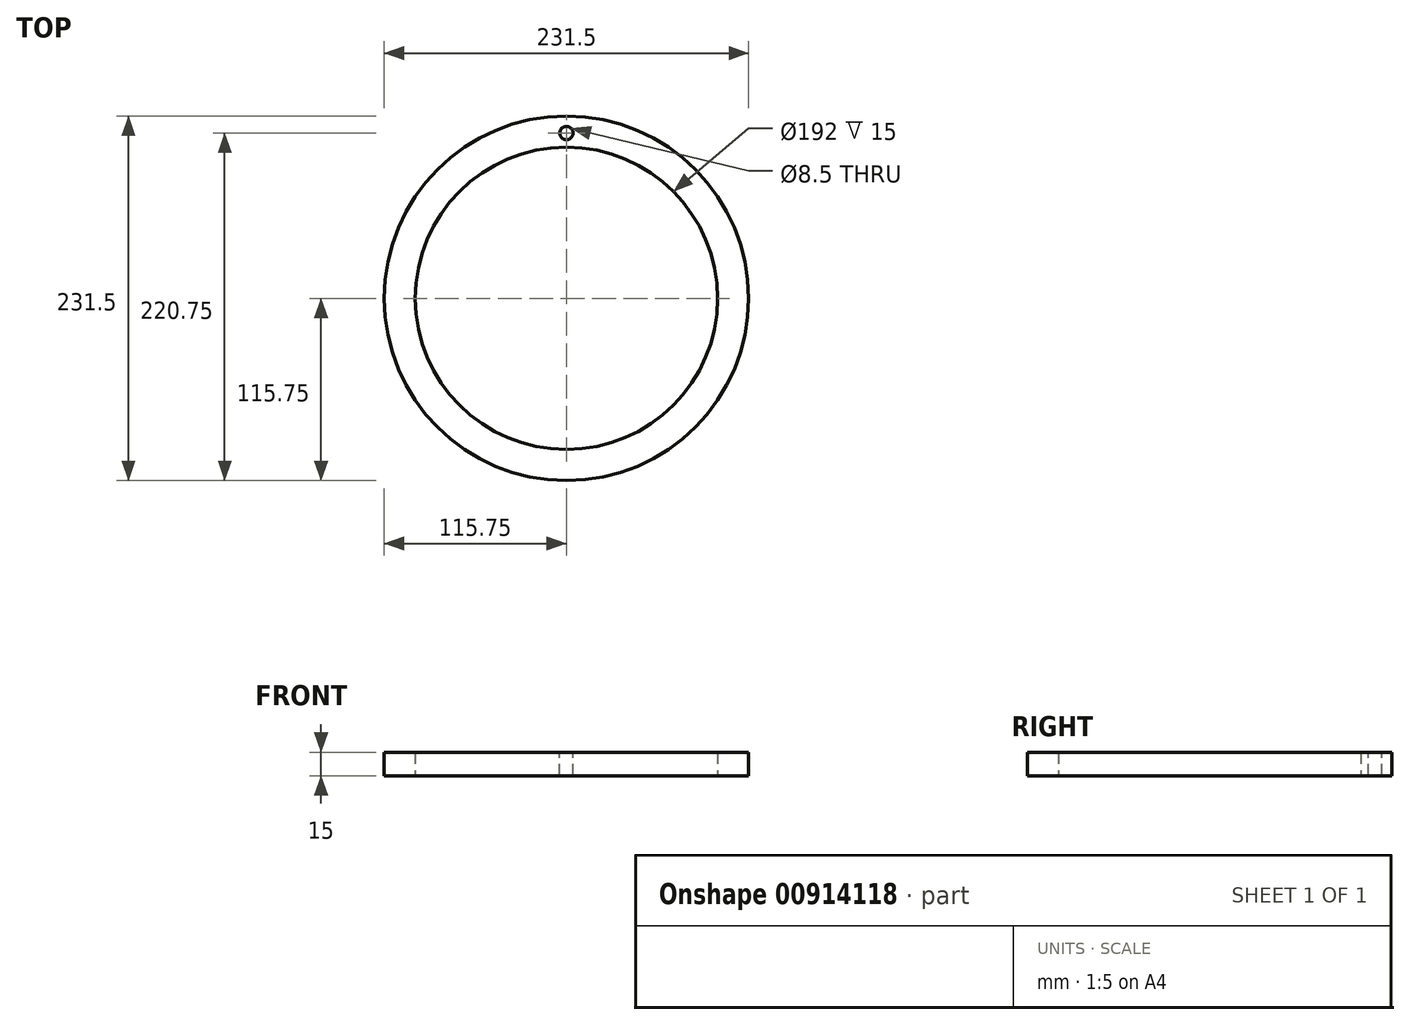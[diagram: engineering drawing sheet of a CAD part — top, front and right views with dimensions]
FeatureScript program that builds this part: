
annotation { "Feature Type Name" : "Feature", "Feature Type Description" : "" }
export const myFeature = defineFeature(function(context is Context, id is Id, definition is map)
    precondition{}
    {
        {
            var Q0;
            Q0=qCreatedBy(makeId("Top.planeOp"),FACE);
            var sketch = newSketch(context, id + "F0", { "sketchPlane" : qUnion([Q0])});
            skCircle(sketch, "E0", {"center": v(0, 0) * mm, "radius": 115.75 * mm});
            skCircle(sketch, "E1", {"center": v(0, 0) * mm, "radius": 96 * mm});
            skSolve(sketch);
        }
        {
            var Q0;
            Q0=makeQuery(id+"F0.imprint","IMPRINT",FACE,{"disambiguationData":[TD([[makeQuery(id+"F0.imprint","IMPRINT",EDGE,{"derivedFrom":sQuery(id+"F0.wireOp",EDGE,"E0")}),1.0]])]});
            extrude(context, id + "F1", {"entities" : qUnion([Q0]), "depth" : 15 * mm, "offsetDistance" : 25 * mm});
        }
        {
            var Q0;
            Q0=makeQuery(id+"F1.opExtrude","CAP_FACE",FACE,{"disambiguationData":[OSD([sQuery(id+"F0.wireOp",EDGE,"E0"),sQuery(id+"F0.wireOp",EDGE,"E1")])],"isStart":false});
            var sketch = newSketch(context, id + "F2", { "sketchPlane" : qUnion([Q0])});
            skPoint(sketch, "E2", {"position": v(0, 105) * mm});
            skSolve(sketch);
        }
        {
            var Q0;
            Q0=sQuery(id+"F2.wireOp",VERTEX,"E2");
            var Q1;
            Q1=makeQuery(id+"F1.opExtrude","SWEPT_BODY",BODY,{"disambiguationData":[OSD([sQuery(id+"F0.wireOp",EDGE,"E0"),sQuery(id+"F0.wireOp",EDGE,"E1")])]});
            hole(context, id + "F3", {"style" : HoleStyle.SIMPLE, "endStyle" : HoleEndStyle.THROUGH, "standardTappedOrClearance" : lookupTablePath({ "standard" : "ISO", "engagement" : "75%", "pitch" : "1.5 mm", "size" : "M10", "type" : "Tapped" }), "standardBlindInLast" : lookupTablePath({ "standard" : "ISO", "fit" : "Normal", "engagement" : "75%", "pitch" : "1.5 mm", "size" : "M10", "type" : "Clearance & tapped" }), "holeDiameter" : 8.5 * mm, "majorDiameter" : 10 * mm, "showTappedDepth" : true, "isTappedThrough" : true, "tappedDepth" : 14 * mm, "tapClearance" : 3, "locations" : qUnion([Q0]), "scope" : qUnion([Q1])});
        }
    });
